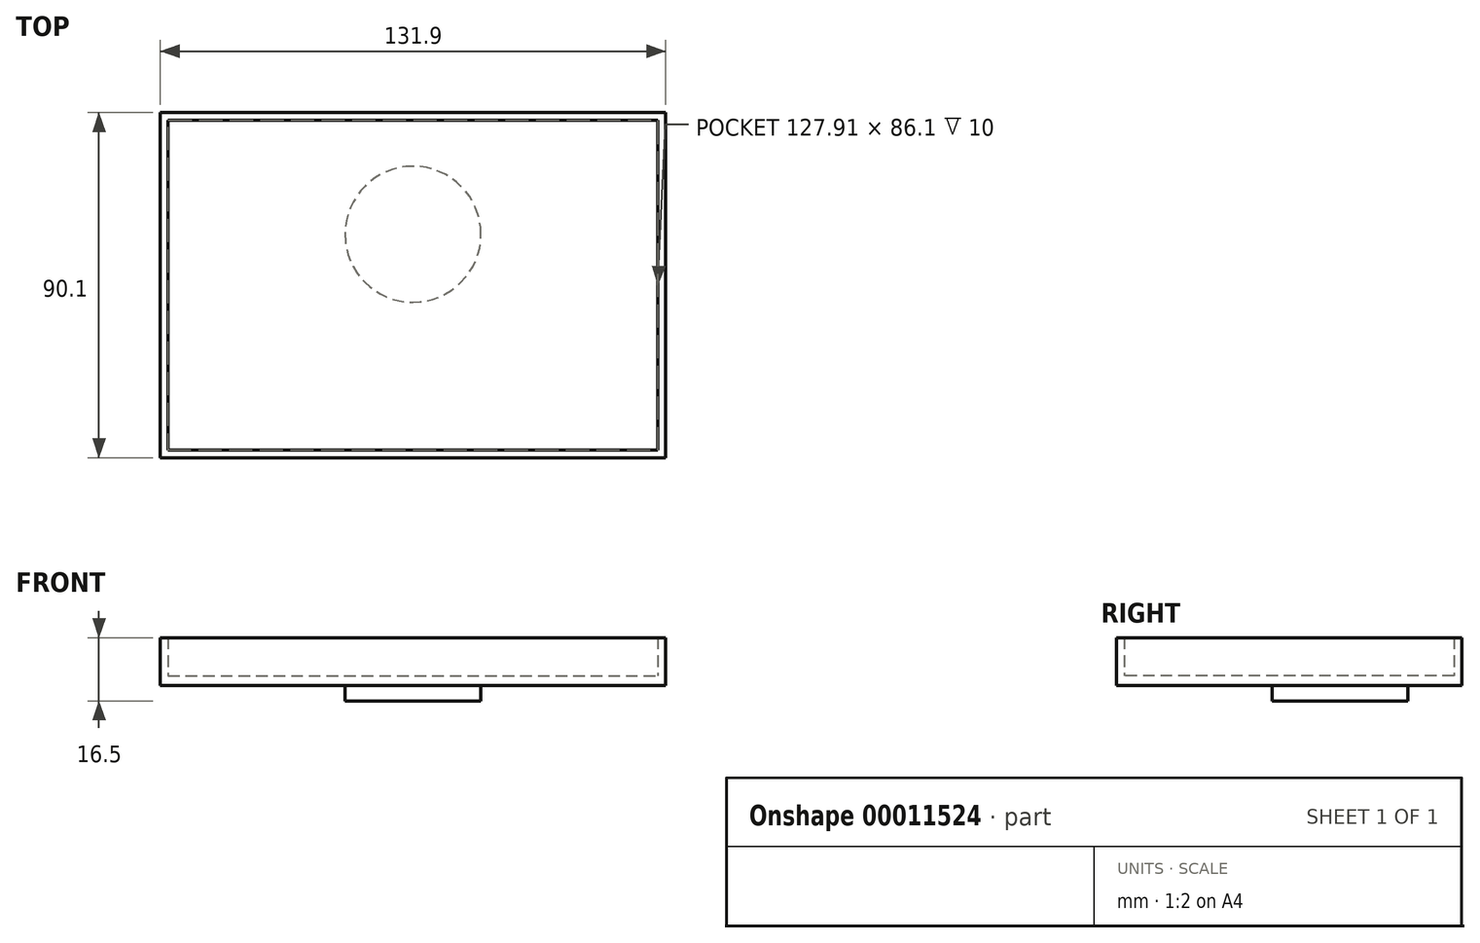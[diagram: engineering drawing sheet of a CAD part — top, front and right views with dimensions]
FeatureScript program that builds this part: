
annotation { "Feature Type Name" : "Feature", "Feature Type Description" : "" }
export const myFeature = defineFeature(function(context is Context, id is Id, definition is map)
    precondition{}
    {
        {
            var Q0;
            Q0=qCreatedBy(makeId("Top.planeOp"),FACE);
            var sketch = newSketch(context, id + "F0", { "sketchPlane" : qUnion([Q0])});
            skCircle(sketch, "E0", {"center": v(0, 0) * mm, "radius": 17.75 * mm});
            skSolve(sketch);
        }
        {
            var Q0;
            Q0 = qSketchRegion(id + "F0", true);
            extrude(context, id + "F1", {"entities" : qUnion([Q0]), "depth" : 4 * mm});
        }
        {
            var Q0;
            Q0=makeQuery(id+"F1.opExtrude","CAP_FACE",FACE,{"disambiguationData":[OSD([sQuery(id+"F0.wireOp",EDGE,"E0")])],"isStart":false});
            var sketch = newSketch(context, id + "F2", { "sketchPlane" : qUnion([Q0])});
            skLineSegment(sketch, "E1.bottom", {"start": v(-65.95, 31.78) * mm, "end": v(65.95, 31.78) * mm});
            skLineSegment(sketch, "E1.top", {"start": v(-65.95, -58.32) * mm, "end": v(65.95, -58.32) * mm});
            skLineSegment(sketch, "E1.left", {"start": v(-65.95, 31.78) * mm, "end": v(-65.95, -58.32) * mm});
            skLineSegment(sketch, "E1.right", {"start": v(65.95, 31.78) * mm, "end": v(65.95, -58.32) * mm});
            skSolve(sketch);
        }
        {
            var Q0;
            Q0=makeQuery(id+"F1.opExtrude","CAP_FACE",FACE,{"disambiguationData":[OSD([sQuery(id+"F0.wireOp",EDGE,"E0")])],"isStart":false});
            var Q1;
            Q1=makeQuery(id+"F2.imprint","IMPRINT",FACE,{"disambiguationData":[TD([[makeQuery(id+"F2.imprint","IMPRINT",EDGE,{"derivedFrom":sQuery(id+"F2.wireOp",EDGE,"E1.bottom")}),-1.0]])]});
            extrude(context, id + "F3", {"entities" : qUnion([Q0, Q1]), "operationType" : NewBodyOperationType.ADD, "depth" : 2.5 * mm});
        }
        {
            var Q0;
            {var subQ0=sQuery(id+"F0.wireOp",EDGE,"E0");Q0=makeQuery(id+"F3.boolean.opBoolean","MERGE",FACE,{"derivedFrom":[makeQuery(id+"F3.opExtrude","CAP_FACE",FACE,{"disambiguationData":[OSD([subQ0])],"isStart":false}),makeQuery(id+"F3.opExtrude","CAP_FACE",FACE,{"disambiguationData":[OSD([subQ0,sQuery(id+"F2.wireOp",EDGE,"E1.bottom"),sQuery(id+"F2.wireOp",EDGE,"E1.top"),sQuery(id+"F2.wireOp",EDGE,"E1.left"),sQuery(id+"F2.wireOp",EDGE,"E1.right")])],"isStart":false})]});}
            var sketch = newSketch(context, id + "F4", { "sketchPlane" : qUnion([Q0])});
            skLineSegment(sketch, "E2.bottom", {"start": v(-65.95, 31.78) * mm, "end": v(65.95, 31.78) * mm});
            skLineSegment(sketch, "E2.top", {"start": v(-65.95, -58.32) * mm, "end": v(65.95, -58.32) * mm});
            skLineSegment(sketch, "E2.left", {"start": v(-65.95, 31.78) * mm, "end": v(-65.95, -58.32) * mm});
            skLineSegment(sketch, "E2.right", {"start": v(65.95, 31.78) * mm, "end": v(65.95, -58.32) * mm});
            skLineSegment(sketch, "E3.bottom", {"start": v(-63.95, 29.78) * mm, "end": v(63.95, 29.78) * mm});
            skLineSegment(sketch, "E3.top", {"start": v(-63.95, -56.32) * mm, "end": v(63.95, -56.32) * mm});
            skLineSegment(sketch, "E3.left", {"start": v(-63.95, 29.78) * mm, "end": v(-63.95, -56.32) * mm});
            skLineSegment(sketch, "E3.right", {"start": v(63.95, 29.78) * mm, "end": v(63.95, -56.32) * mm});
            skSolve(sketch);
        }
        {
            var Q0;
            Q0 = qSketchRegion(id + "F4", true);
            extrude(context, id + "F5", {"entities" : qUnion([Q0]), "operationType" : NewBodyOperationType.ADD, "depth" : 10 * mm});
        }
    });
